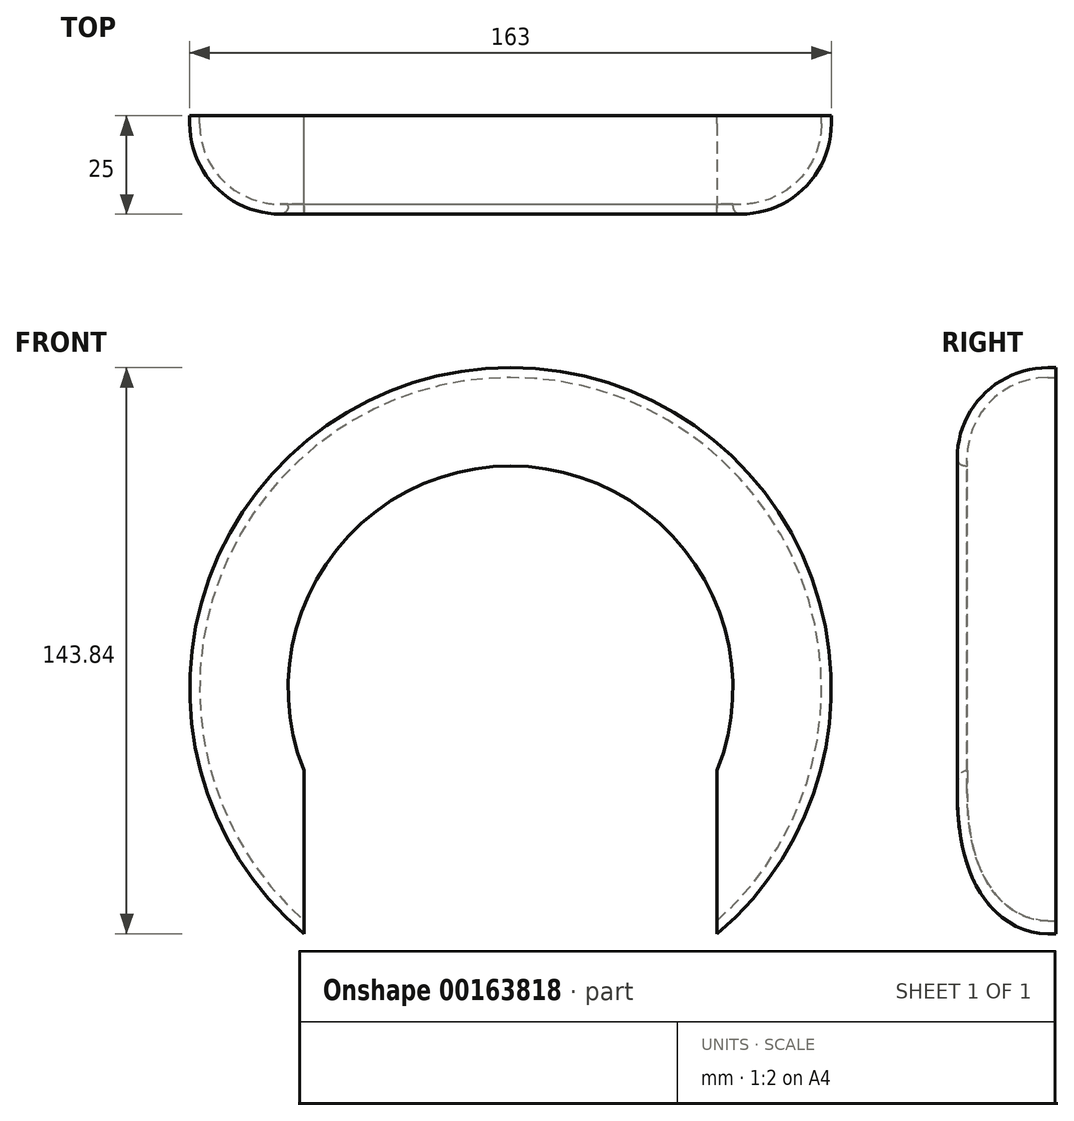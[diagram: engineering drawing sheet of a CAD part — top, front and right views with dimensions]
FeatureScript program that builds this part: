
annotation { "Feature Type Name" : "Feature", "Feature Type Description" : "" }
export const myFeature = defineFeature(function(context is Context, id is Id, definition is map)
    precondition{}
    {
        {
            var Q0;
            Q0=qCreatedBy(makeId("Front.planeOp"),FACE);
            var sketch = newSketch(context, id + "F0", { "sketchPlane" : qUnion([Q0])});
            skArc(sketch, "E0", {"start": v(52.5, -62.34) * mm, "mid": v(0, 81.5) * mm, "end": v(-52.5, -62.34) * mm});
            skArc(sketch, "E1", {"start": v(52.5, -20.88) * mm, "mid": v(0, 56.5) * mm, "end": v(-52.5, -20.88) * mm});
            skLineSegment(sketch, "E2.top", {"start": v(-52.5, -90) * mm, "end": v(52.5, -90) * mm});
            skLineSegment(sketch, "E2.left", {"start": v(-52.5, -20.88) * mm, "end": v(-52.5, -62.34) * mm});
            skLineSegment(sketch, "E2.right", {"start": v(52.5, -20.88) * mm, "end": v(52.5, -62.34) * mm});
            skSolve(sketch);
        }
        {
            var Q0;
            Q0=makeQuery(id+"F0.imprint","IMPRINT",FACE,{"disambiguationData":[TD([[makeQuery(id+"F0.imprint","IMPRINT",EDGE,{"derivedFrom":sQuery(id+"F0.wireOp",EDGE,"E0")}),1.0]])]});
            extrude(context, id + "F1", {"entities" : qUnion([Q0]), "depth" : 25 * mm});
        }
        {
            var Q0;
            Q0=makeQuery(id+"F1.opExtrude","CAP_EDGE",EDGE,{"disambiguationData":[OSD([sQuery(id+"F0.wireOp",EDGE,"E0")])],"isStart":false});
            fillet(context, id + "F2", {"entities" : qUnion([Q0]), "radius" : 23 * mm, "tangentPropagation" : true, "allowEdgeOverflow" : false});
        }
        {
            var Q0;
            Q0=makeQuery(id+"F1.opExtrude","CAP_EDGE",EDGE,{"disambiguationData":[OSD([sQuery(id+"F0.wireOp",EDGE,"E1")])],"isStart":false});
            fillet(context, id + "F3", {"entities" : qUnion([Q0]), "radius" : 2 * mm, "tangentPropagation" : true, "allowEdgeOverflow" : false});
        }
        {
            var Q0;
            Q0=makeQuery(id+"F1.opExtrude","SWEPT_FACE",FACE,{"disambiguationData":[OSD([sQuery(id+"F0.wireOp",EDGE,"E1")])]});
            var Q1;
            Q1=makeQuery(id+"F1.opExtrude","SWEPT_FACE",FACE,{"disambiguationData":[OSD([sQuery(id+"F0.wireOp",EDGE,"E2.left")])]});
            var Q2;
            Q2=makeQuery(id+"F1.opExtrude","CAP_FACE",FACE,{"disambiguationData":[OSD([sQuery(id+"F0.wireOp",EDGE,"E0"),sQuery(id+"F0.wireOp",EDGE,"E1"),sQuery(id+"F0.wireOp",EDGE,"E2.left"),sQuery(id+"F0.wireOp",EDGE,"E2.right")])],"isStart":true});
            var Q3;
            Q3=makeQuery(id+"F1.opExtrude","SWEPT_FACE",FACE,{"disambiguationData":[OSD([sQuery(id+"F0.wireOp",EDGE,"E2.right")])]});
            shell(context, id + "F4", {"entities" : qUnion([Q0, Q1, Q2, Q3]), "thickness" : 2.5 * mm});
        }
    });
